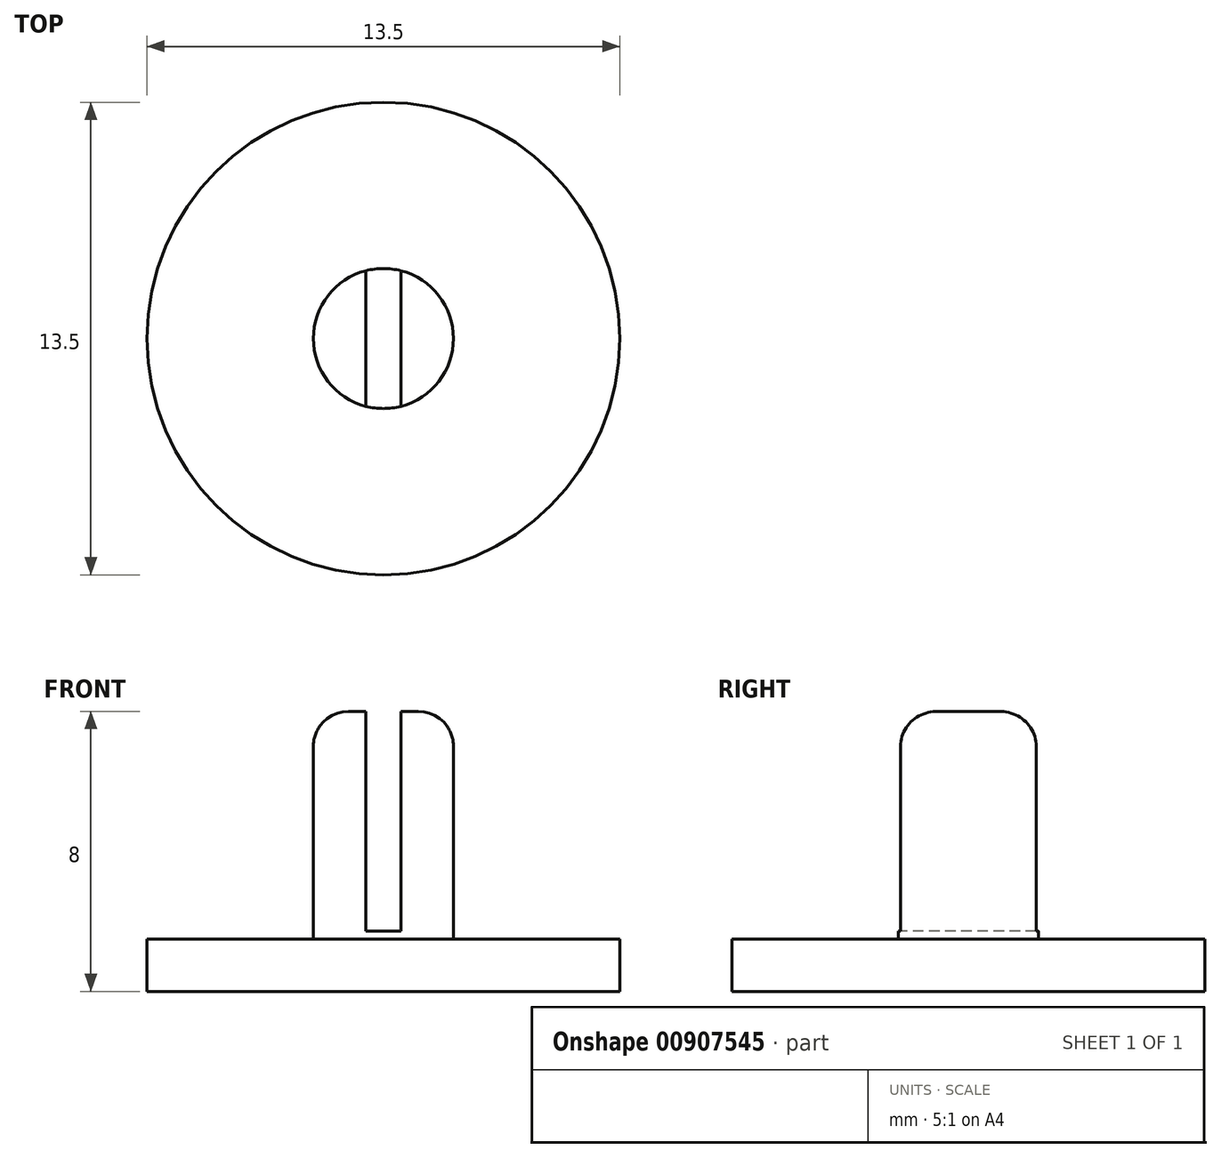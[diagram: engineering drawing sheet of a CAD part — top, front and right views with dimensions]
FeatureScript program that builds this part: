
annotation { "Feature Type Name" : "Feature", "Feature Type Description" : "" }
export const myFeature = defineFeature(function(context is Context, id is Id, definition is map)
    precondition{}
    {
        {
            var Q0;
            Q0=qCreatedBy(makeId("Top.planeOp"),FACE);
            var sketch = newSketch(context, id + "F0", { "sketchPlane" : qUnion([Q0])});
            skCircle(sketch, "E0", {"center": v(0, 0) * mm, "radius": 6.75 * mm});
            skSolve(sketch);
        }
        {
            var Q0;
            Q0=makeQuery(id+"F0.imprint","IMPRINT",FACE,{"disambiguationData":[TD([[makeQuery(id+"F0.imprint","IMPRINT",EDGE,{"derivedFrom":sQuery(id+"F0.wireOp",EDGE,"E0")}),1.0]])]});
            extrude(context, id + "F1", {"entities" : qUnion([Q0]), "depth" : 1.5 * mm, "offsetDistance" : 25 * mm});
        }
        {
            var Q0;
            Q0=makeQuery(id+"F1.opExtrude","CAP_FACE",FACE,{"disambiguationData":[OSD([sQuery(id+"F0.wireOp",EDGE,"E0")])],"isStart":false});
            var sketch = newSketch(context, id + "F2", { "sketchPlane" : qUnion([Q0])});
            skLineSegment(sketch, "E1.bottom", {"start": v(2, 2) * mm, "end": v(-2, 2) * mm});
            skLineSegment(sketch, "E1.top", {"start": v(2, -2) * mm, "end": v(-2, -2) * mm});
            skLineSegment(sketch, "E1.left", {"start": v(2, 2) * mm, "end": v(2, -2) * mm});
            skLineSegment(sketch, "E1.right", {"start": v(-2, 2) * mm, "end": v(-2, -2) * mm});
            skPoint(sketch, "E1.middle", {"position": v(0, 0) * mm});
            skSolve(sketch);
        }
        {
            var Q0;
            Q0 = qSketchRegion(id + "F2", true);
            extrude(context, id + "F3", {"entities" : qUnion([Q0]), "operationType" : NewBodyOperationType.ADD, "depth" : 6.5 * mm, "offsetDistance" : 25 * mm});
        }
        {
            var Q0;
            Q0=makeQuery(id+"F3.opExtrude","SWEPT_FACE",FACE,{"disambiguationData":[OSD([sQuery(id+"F2.wireOp",EDGE,"E1.top")])]});
            var sketch = newSketch(context, id + "F4", { "sketchPlane" : qUnion([Q0])});
            skSolve(sketch);
        }
        {
            var Q0;
            {var subQ0=sQuery(id+"F2.wireOp",EDGE,"E1.top");Q0=makeQuery(id+"F4.imprint","IMPRINT",FACE,{"disambiguationData":[TD([[makeQuery(id+"F4.imprint","IMPRINT",EDGE,{"derivedFrom":makeQuery(id+"F3.opExtrude","CAP_EDGE",EDGE,{"disambiguationData":[OSD([subQ0])],"isStart":false})}),1.0]])]});}
            var sketch = newSketch(context, id + "F5", { "sketchPlane" : qUnion([Q0])});
            skLineSegment(sketch, "E2.bottom", {"start": v(-0.5, 1.73) * mm, "end": v(0.5, 1.73) * mm});
            skLineSegment(sketch, "E2.top", {"start": v(-0.5, 8.71) * mm, "end": v(0.5, 8.71) * mm});
            skLineSegment(sketch, "E2.left", {"start": v(-0.5, 1.73) * mm, "end": v(-0.5, 8.71) * mm});
            skLineSegment(sketch, "E2.right", {"start": v(0.5, 1.73) * mm, "end": v(0.5, 8.71) * mm});
            skSolve(sketch);
        }
        {
            var Q0;
            {var subQ0=sQuery(id+"F5.wireOp",EDGE,"E2.bottom");Q0=makeQuery(id+"F5.imprint","IMPRINT",FACE,{"disambiguationData":[TD([[makeQuery(id+"F5.imprint","IMPRINT",EDGE,{"derivedFrom":subQ0}),1.0]])]});}
            extrude(context, id + "F6", {"entities" : qUnion([Q0]), "operationType" : NewBodyOperationType.REMOVE, "oppositeDirection" : true, "depth" : 25 * mm, "offsetDistance" : 25 * mm});
        }
        {
            var Q0;
            Q0=makeQuery(id+"F3.opExtrude","SWEPT_EDGE",EDGE,{"disambiguationData":[OSD([sQuery(id+"F2.wireOp",EDGE,"E1.top"),sQuery(id+"F2.wireOp",EDGE,"E1.left")])]});
            var Q1;
            Q1=makeQuery(id+"F3.opExtrude","SWEPT_EDGE",EDGE,{"disambiguationData":[OSD([sQuery(id+"F2.wireOp",EDGE,"E1.bottom"),sQuery(id+"F2.wireOp",EDGE,"E1.left")])]});
            var Q2;
            Q2=makeQuery(id+"F3.opExtrude","SWEPT_EDGE",EDGE,{"disambiguationData":[OSD([sQuery(id+"F2.wireOp",EDGE,"E1.bottom"),sQuery(id+"F2.wireOp",EDGE,"E1.right")])]});
            var Q3;
            Q3=makeQuery(id+"F3.opExtrude","SWEPT_EDGE",EDGE,{"disambiguationData":[OSD([sQuery(id+"F2.wireOp",EDGE,"E1.top"),sQuery(id+"F2.wireOp",EDGE,"E1.right")])]});
            fillet(context, id + "F7", {"entities" : qUnion([Q0, Q1, Q2, Q3]), "radius" : 2 * mm, "tangentPropagation" : true, "allowEdgeOverflow" : false});
        }
        {
            var Q0;
            {var subQ0=sQuery(id+"F2.wireOp",EDGE,"E1.bottom");var subQ1=sQuery(id+"F2.wireOp",EDGE,"E1.top");var subQ2=sQuery(id+"F2.wireOp",EDGE,"E1.left");Q0=makeQuery(id+"F7.opFillet","BLEND_EDGE",EDGE,{"blendedFrom":[makeQuery(id+"F3.opExtrude","SWEPT_EDGE",EDGE,{"disambiguationData":[OSD([subQ0,subQ2])]}),makeQuery(id+"F6.boolean.opBoolean","SPLIT",FACE,{"disambiguationData":[TD([makeQuery(id+"F3.opExtrude","SWEPT_FACE",FACE,{"disambiguationData":[OSD([subQ2])]})])],"derivedFrom":makeQuery(id+"F3.opExtrude","CAP_FACE",FACE,{"disambiguationData":[OSD([subQ0,subQ1,subQ2,sQuery(id+"F2.wireOp",EDGE,"E1.right")])],"isStart":false})})],"blendedInto":[makeQuery(id+"F6.boolean.opBoolean","SPLIT",FACE,{"disambiguationData":[TD([makeQuery(id+"F3.opExtrude","SWEPT_FACE",FACE,{"disambiguationData":[OSD([subQ2])]})])],"derivedFrom":makeQuery(id+"F3.opExtrude","CAP_FACE",FACE,{"disambiguationData":[OSD([subQ0,subQ1,subQ2,sQuery(id+"F2.wireOp",EDGE,"E1.right")])],"isStart":false})})]});}
            var Q1;
            {var subQ0=sQuery(id+"F2.wireOp",EDGE,"E1.bottom");var subQ1=sQuery(id+"F2.wireOp",EDGE,"E1.right");var subQ2=sQuery(id+"F2.wireOp",EDGE,"E1.top");Q1=makeQuery(id+"F7.opFillet","BLEND_EDGE",EDGE,{"blendedFrom":[makeQuery(id+"F3.opExtrude","SWEPT_EDGE",EDGE,{"disambiguationData":[OSD([subQ0,subQ1])]}),makeQuery(id+"F6.boolean.opBoolean","SPLIT",FACE,{"disambiguationData":[TD([makeQuery(id+"F3.opExtrude","SWEPT_FACE",FACE,{"disambiguationData":[OSD([subQ1])]})])],"derivedFrom":makeQuery(id+"F3.opExtrude","CAP_FACE",FACE,{"disambiguationData":[OSD([subQ0,subQ2,sQuery(id+"F2.wireOp",EDGE,"E1.left"),subQ1])],"isStart":false})})],"blendedInto":[makeQuery(id+"F6.boolean.opBoolean","SPLIT",FACE,{"disambiguationData":[TD([makeQuery(id+"F3.opExtrude","SWEPT_FACE",FACE,{"disambiguationData":[OSD([subQ1])]})])],"derivedFrom":makeQuery(id+"F3.opExtrude","CAP_FACE",FACE,{"disambiguationData":[OSD([subQ0,subQ2,sQuery(id+"F2.wireOp",EDGE,"E1.left"),subQ1])],"isStart":false})})]});}
            fillet(context, id + "F8", {"entities" : qUnion([Q0, Q1]), "radius" : 1 * mm, "tangentPropagation" : true, "allowEdgeOverflow" : false});
        }
    });
